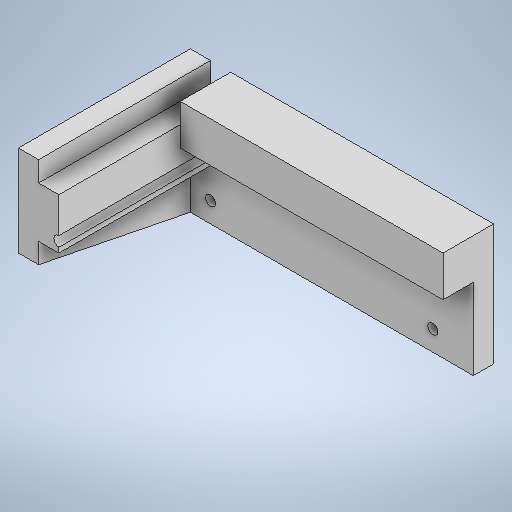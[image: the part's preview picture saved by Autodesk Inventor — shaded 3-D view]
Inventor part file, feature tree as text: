
AUTODESK INVENTOR PART (.ipt)
format: ipt  version: 2025.3 (Build 293356000, 356)  size: 550,912 bytes
history: native  units: mm
features: extrude x4, sketch x2, other x1, projected_geometry x1
ambient origin geometry x8: Origin, YZ Plane, XZ Plane, XY Plane, X Axis, Y Axis, Z Axis, Center Point
bodies: Body1 (feature_tree)
feature tree (8):
  other  "솔리드1"
  sketch  "스케치1"
  extrude  "돌출1"  Depth=5.0mm
  extrude  "돌출2"  Depth=30.0mm
  extrude  "돌출3"  Depth=20.0mm
  extrude  "돌출4"  Depth=20.0mm
  sketch  "스케치2"
  projected_geometry  "투영된 루프1"
